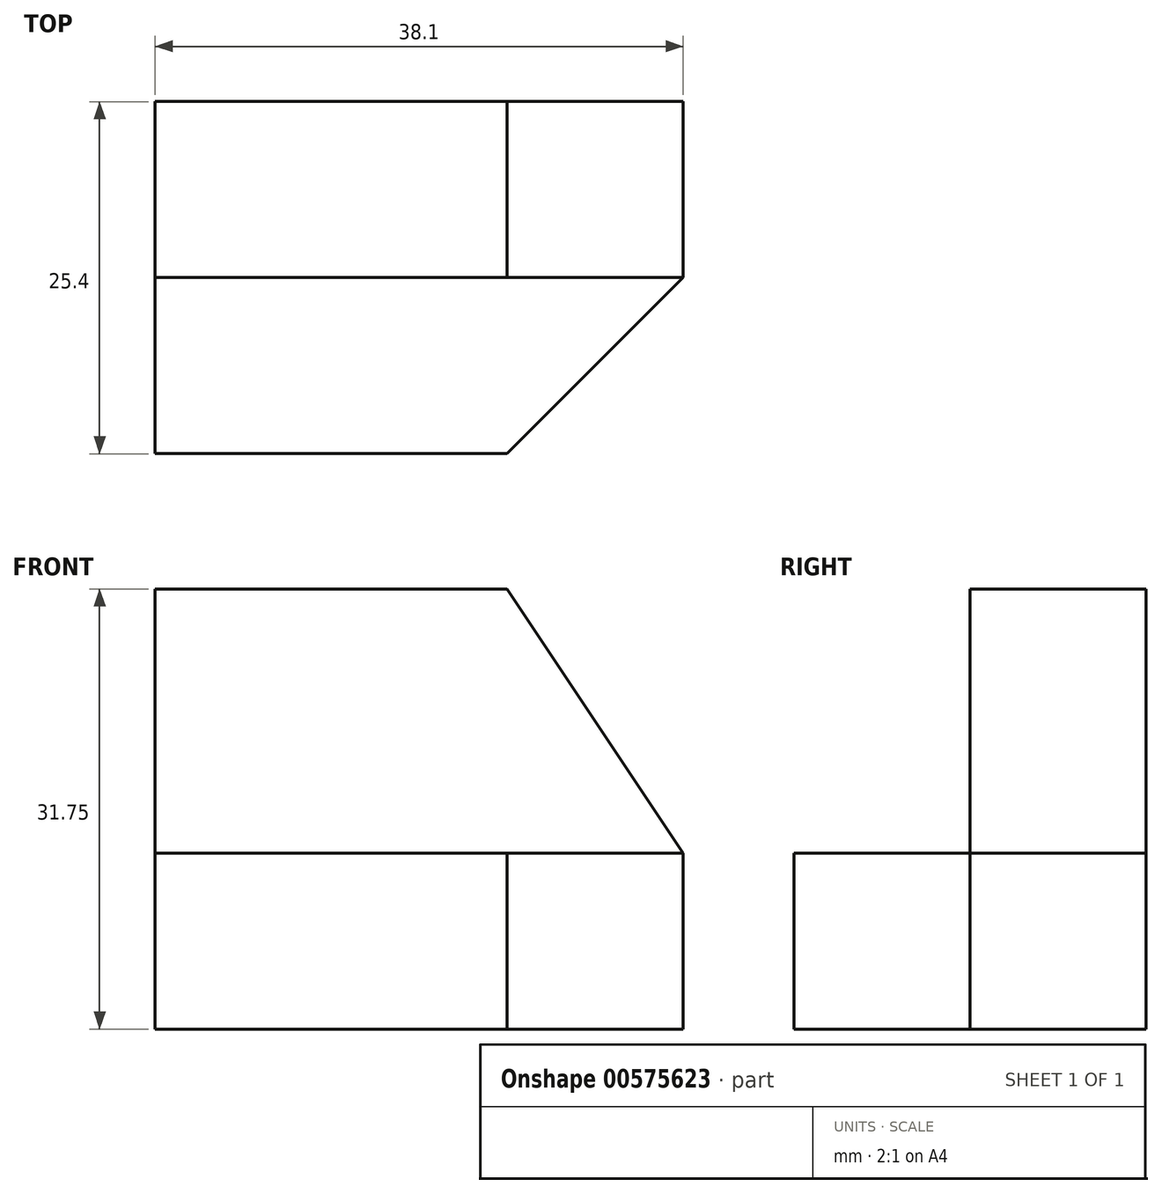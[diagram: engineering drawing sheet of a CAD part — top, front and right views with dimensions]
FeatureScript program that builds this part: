
annotation { "Feature Type Name" : "Feature", "Feature Type Description" : "" }
export const myFeature = defineFeature(function(context is Context, id is Id, definition is map)
    precondition{}
    {
        {
            var Q0;
            Q0=qCreatedBy(makeId("Right.planeOp"),FACE);
            var sketch = newSketch(context, id + "F0", { "sketchPlane" : qUnion([Q0])});
            skLineSegment(sketch, "E0", {"start": v(-37.9, 49.25) * mm, "end": v(-37.9, 30.2) * mm});
            skLineSegment(sketch, "E1", {"start": v(-37.9, 49.25) * mm, "end": v(-25.2, 49.25) * mm});
            skLineSegment(sketch, "E2", {"start": v(-25.2, 49.25) * mm, "end": v(-25.2, 17.5) * mm});
            skLineSegment(sketch, "E3", {"start": v(-25.2, 17.5) * mm, "end": v(-50.6, 17.5) * mm});
            skLineSegment(sketch, "E4", {"start": v(-37.9, 30.2) * mm, "end": v(-50.6, 30.2) * mm});
            skLineSegment(sketch, "E5", {"start": v(-50.6, 30.2) * mm, "end": v(-50.6, 17.5) * mm});
            skSolve(sketch);
        }
        {
            var Q0;
            Q0 = qSketchRegion(id + "F0", true);
            extrude(context, id + "F1", {"entities" : qUnion([Q0]), "depth" : 38.1 * mm, "offsetDistance" : 25.4 * mm});
        }
        {
            var Q0;
            Q0=makeQuery(id+"F1.opExtrude","SWEPT_FACE",FACE,{"disambiguationData":[OSD([sQuery(id+"F0.wireOp",EDGE,"E0")])]});
            var sketch = newSketch(context, id + "F2", { "sketchPlane" : qUnion([Q0])});
            skLineSegment(sketch, "E6", {"start": v(25.4, 49.25) * mm, "end": v(38.1, 30.2) * mm});
            skSolve(sketch);
        }
        {
            var Q0;
            Q0 = qSketchRegion(id + "F2", true);
            var Q1;
            {var subQ0=sQuery(id+"F2.wireOp",EDGE,"E6");Q1=makeQuery(id+"F2.imprint","IMPRINT",FACE,{"disambiguationData":[TD([[makeQuery(id+"F2.imprint","IMPRINT",EDGE,{"derivedFrom":subQ0}),1.0]])]});}
            extrude(context, id + "F3", {"entities" : qUnion([Q0, Q1]), "operationType" : NewBodyOperationType.REMOVE, "endBound" : BoundingType.THROUGH_ALL, "oppositeDirection" : true, "depth" : 25.4 * mm, "offsetDistance" : 25.4 * mm});
        }
        {
            var Q0;
            Q0=makeQuery(id+"F1.opExtrude","SWEPT_FACE",FACE,{"disambiguationData":[OSD([sQuery(id+"F0.wireOp",EDGE,"E4")])]});
            var sketch = newSketch(context, id + "F4", { "sketchPlane" : qUnion([Q0])});
            skLineSegment(sketch, "E7", {"start": v(38.1, -37.9) * mm, "end": v(25.4, -50.6) * mm});
            skSolve(sketch);
        }
        {
            var Q0;
            Q0 = qSketchRegion(id + "F4", true);
            var Q1;
            {var subQ0=sQuery(id+"F4.wireOp",EDGE,"E7");Q1=makeQuery(id+"F4.imprint","IMPRINT",FACE,{"disambiguationData":[TD([[makeQuery(id+"F4.imprint","IMPRINT",EDGE,{"derivedFrom":subQ0}),1.0]])]});}
            extrude(context, id + "F5", {"entities" : qUnion([Q0, Q1]), "operationType" : NewBodyOperationType.REMOVE, "endBound" : BoundingType.THROUGH_ALL, "oppositeDirection" : true, "depth" : 25.4 * mm, "offsetDistance" : 25.4 * mm});
        }
    });
